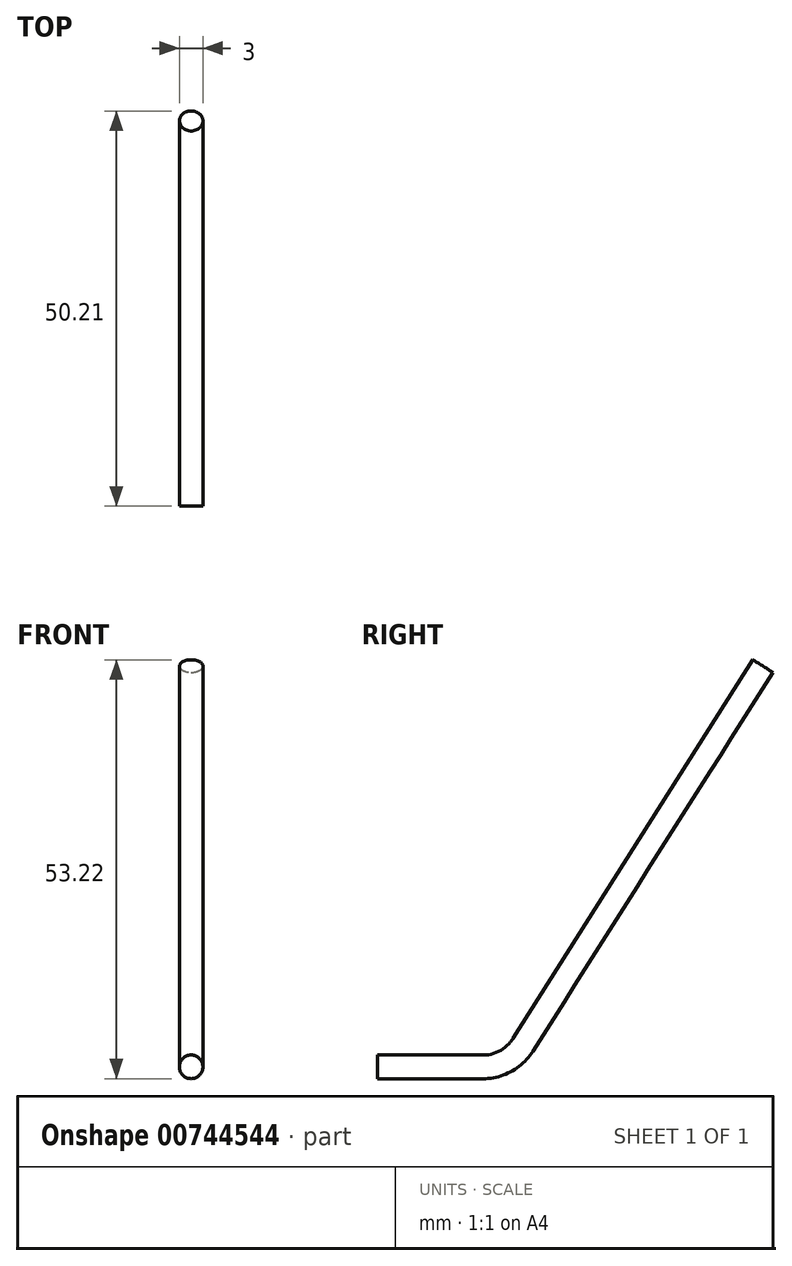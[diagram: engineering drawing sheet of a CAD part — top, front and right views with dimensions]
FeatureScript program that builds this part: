
annotation { "Feature Type Name" : "Feature", "Feature Type Description" : "" }
export const myFeature = defineFeature(function(context is Context, id is Id, definition is map)
    precondition{}
    {
        {
            var Q0;
            Q0=qCreatedBy(makeId("Front.planeOp"),FACE);
            var sketch = newSketch(context, id + "F0", { "sketchPlane" : qUnion([Q0])});
            skCircle(sketch, "E0", {"center": v(0, 0) * mm, "radius": 1.5 * mm});
            skSolve(sketch);
        }
        {
            var Q0;
            Q0=qCreatedBy(makeId("Right.planeOp"),FACE);
            var sketch = newSketch(context, id + "F1", { "sketchPlane" : qUnion([Q0])});
            skLineSegment(sketch, "E1", {"start": v(0, 0) * mm, "end": v(0.7, 0) * mm});
            skLineSegment(sketch, "E2", {"start": v(5.77, 2.79) * mm, "end": v(9.07, 8) * mm});
            skPoint(sketch, "E3.visualSharp", {"position": v(4, 0) * mm});
            skArc(sketch, "E3.filletArc", {"start": v(0.7, 0) * mm, "mid": v(3.6, 0.74) * mm, "end": v(5.77, 2.79) * mm});
            skSolve(sketch);
        }
        {
            var Q0;
            Q0=makeQuery(id+"F0.imprint","IMPRINT",FACE,{"disambiguationData":[TD([[makeQuery(id+"F0.imprint","IMPRINT",EDGE,{"derivedFrom":sQuery(id+"F0.wireOp",EDGE,"E0")}),1.0]])]});
            var Q1;
            Q1=sQuery(id+"F1.wireOp",EDGE,"E1");
            var Q2;
            Q2=sQuery(id+"F1.wireOp",EDGE,"E3.filletArc");
            var Q3;
            Q3=sQuery(id+"F1.wireOp",EDGE,"E2");
            sweep(context, id + "F2", {"profiles" : qUnion([Q0]), "path" : qUnion([Q1, Q2, Q3])});
        }
        {
            var Q0;
            Q0=makeQuery(id+"F0.imprint","IMPRINT",FACE,{"disambiguationData":[TD([[makeQuery(id+"F0.imprint","IMPRINT",EDGE,{"derivedFrom":sQuery(id+"F0.wireOp",EDGE,"E0")}),1.0]])]});
            extrude(context, id + "F3", {"entities" : qUnion([Q0]), "operationType" : NewBodyOperationType.ADD, "depth" : 12.7 * mm, "offsetDistance" : 25.4 * mm});
        }
        {
            var Q0;
            Q0=makeQuery(id+"F2.opSweep","CAP_FACE",FACE,{"disambiguationData":[OSD([sQuery(id+"F0.wireOp",EDGE,"E0"),sQuery(id+"F1.wireOp",VERTEX,"E2.end")])],"isStart":false});
            extrude(context, id + "F4", {"entities" : qUnion([Q0]), "operationType" : NewBodyOperationType.ADD, "depth" : 50.8 * mm, "offsetDistance" : 25.4 * mm});
        }
    });
